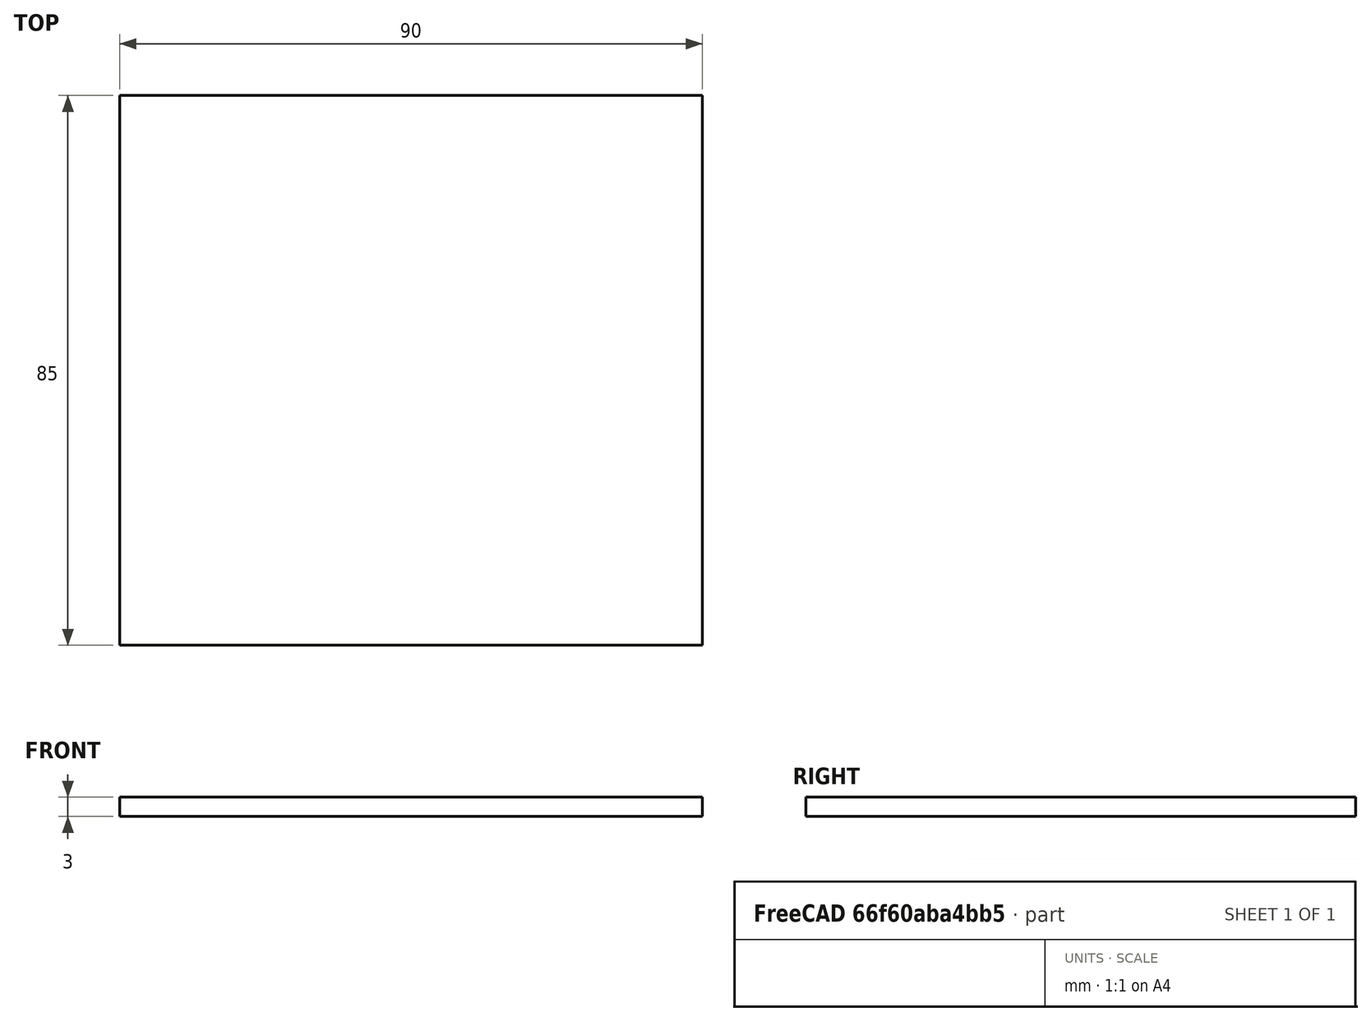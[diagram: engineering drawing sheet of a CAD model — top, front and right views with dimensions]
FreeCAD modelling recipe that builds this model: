
FCSTD DOCUMENT  (FreeCAD 2023.131R26244 +5365 (Git))
Label: raspberry-pi-plate
License: All rights reserved
LicenseURL: http://en.wikipedia.org/wiki/All_rights_reserved
objects: Sketcher::SketchObject×2, PartDesign::Pad×1, PartDesign::Body×1
note: 8 computed .brp shape members not serialized (recipe doc carries the construction recipe); baked Part::Feature solids carry a one-line shape summary decoded from their .brp

FEATURE [Sketcher::SketchObject] Sketch
  ArcFitTolerance = 1e-06
  AttachmentSupport = -> [XY_Plane]
  ExternalBSplineMaxDegree = 5
  ExternalBSplineTolerance = 0.0001
  FullyConstrained = true
  InternalTolerance = 1e-06
  InvalidShape = false
  MakeInternals = false
  MapMode = 5
  Support = -> [XY_Plane]
  TreeRank = 11
  ValidateShape = true
  sketch-geometry (4):
    g0: LineSegment StartX=-45 StartY=42.5 StartZ=0 EndX=45 EndY=42.5 EndZ=0
    g1: LineSegment StartX=45 StartY=42.5 StartZ=0 EndX=45 EndY=-42.5 EndZ=0
    g2: LineSegment StartX=45 StartY=-42.5 StartZ=0 EndX=-45 EndY=-42.5 EndZ=0
    g3: LineSegment StartX=-45 StartY=-42.5 StartZ=0 EndX=-45 EndY=42.5 EndZ=0
  constraints (11):
    c: Coincident(g0,g1)
    c: Coincident(g1,g2)
    c: Coincident(g2,g3)
    c: Coincident(g3,g0)
    c: Horizontal(g0)
    c: Horizontal(g2)
    c: Vertical(g1)
    c: Vertical(g3)
    c: DistanceX(g2,g2) = 90
    c: DistanceY(g3,g3) = 85
    c: Symmetric(g0,g2,g-1)
FEATURE [PartDesign::Pad] Pad
  AddSubType = 0
  AlongSketchNormal = false
  AutoTaperInnerAngle = true
  CheckUpToFaceLimits = true
  ClaimChildren = false
  Direction = (0,0,1)
  Fit = 0
  FitJoin = 0
  InnerFit = 0
  InnerFitJoin = 0
  InvalidShape = false
  Length = 3
  Length2 = 100
  Linearize = true
  NewSolid = false
  Profile = -> Sketch
  Suppress = false
  TaperInnerAngle = 0
  TaperInnerAngleRev = 0
  TreeRank = 12
  Type = 0
  ValidateShape = true
  _ProfileBasedVersion = 1
FEATURE [Sketcher::SketchObject] Sketch001
  ArcFitTolerance = 1e-06
  AttachmentSupport = -> [Pad]
  ExternalBSplineMaxDegree = 5
  ExternalBSplineTolerance = 0.0001
  ExternalGeometry = -> [Pad]
  FullyConstrained = false
  InternalTolerance = 1e-06
  InvalidShape = false
  MakeInternals = false
  MapMode = 5
  Placement = pos=(0,0,3) rot=(0,0,1;0rad)
  Support = -> [Pad]
  TreeRank = 13
  ValidateShape = true
  sketch-geometry (4):
    g0: Circle CenterX=-25 CenterY=-14.3872 CenterZ=0 NormalX=0 NormalY=0 NormalZ=1 AngleXU=0 Radius=1.5
    g1: Circle CenterX=25 CenterY=-14.3872 CenterZ=0 NormalX=0 NormalY=0 NormalZ=1 AngleXU=0 Radius=1.5
    g2: Circle CenterX=37 CenterY=10.6128 CenterZ=0 NormalX=0 NormalY=0 NormalZ=1 AngleXU=0 Radius=1.5
    g3: Circle CenterX=-37 CenterY=10.6128 CenterZ=0 NormalX=0 NormalY=0 NormalZ=1 AngleXU=0 Radius=1.5
  constraints (9):
    c: Equal(g1,g0)
    c: Symmetric(g0,g1,g-2)
    c: Diameter(g0) = 3
    c: DistanceX(g0,g1) = 50
    c: Equal(g3,g2)
    c: Equal(g2,g0)
    c: Symmetric(g3,g2,g-2)
    c: DistanceX(g3,g2) = 74
    c: DistanceY(g0,g3) = 25
FEATURE [PartDesign::Body] Body
  AutoGroupSolids = false
  ClaimAllChildren = false
  ExportMode = 0
  Group = -> [Sketch,Pad,Sketch001]
  InvalidShape = false
  Origin = -> Origin
  Tip = -> Pad
  TreeRank = 10
  ValidateShape = true
  _ExportChildren = -> [Pad,Sketch001]
  _GroupVersion = 1
